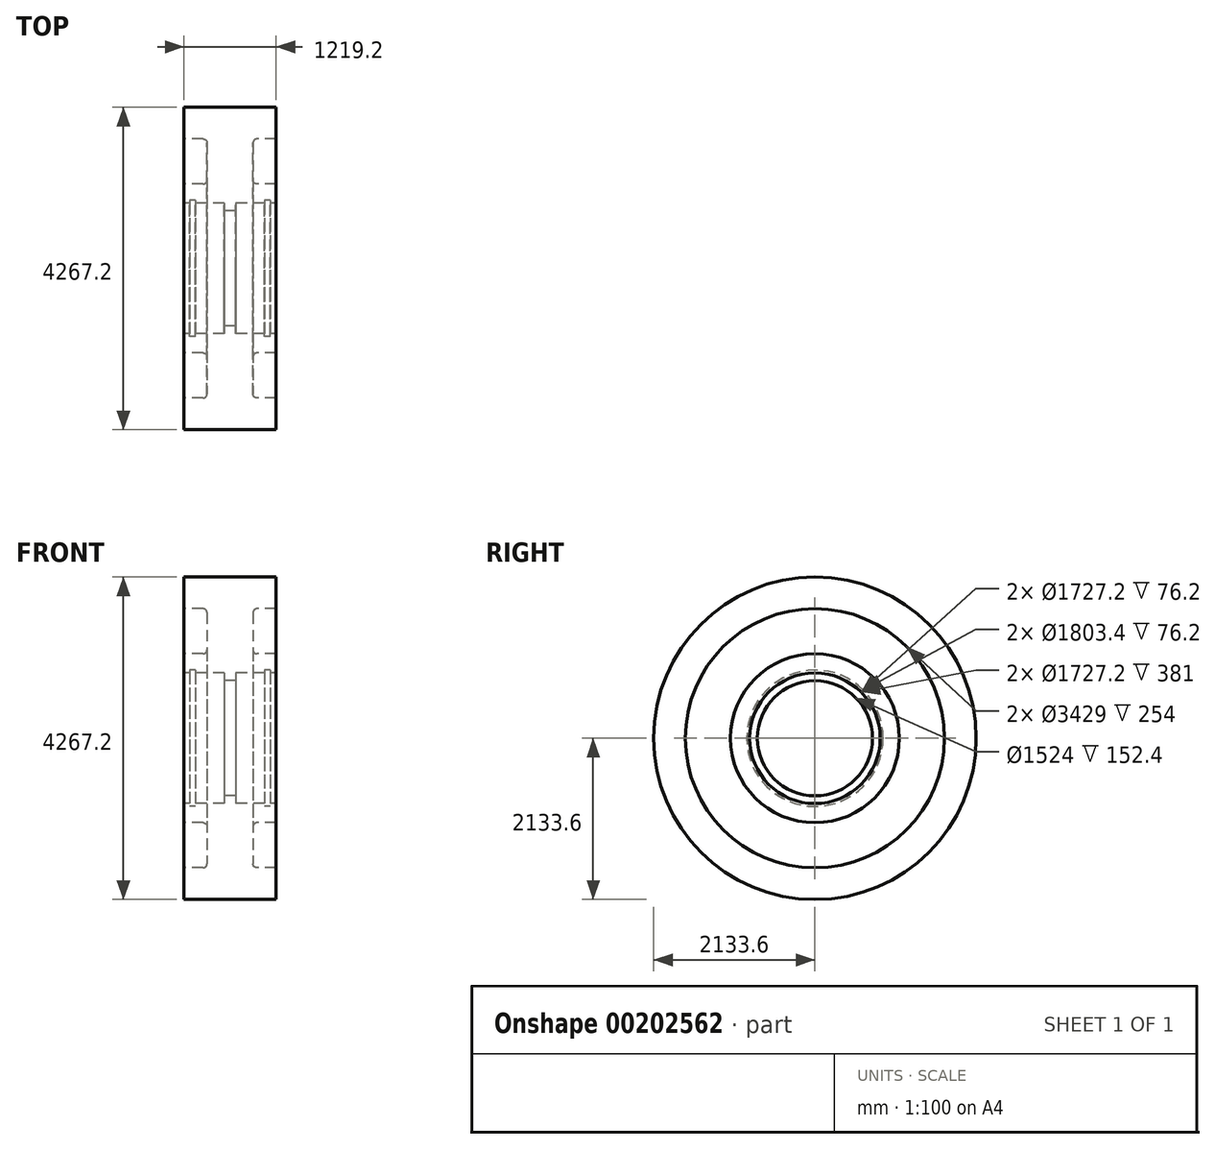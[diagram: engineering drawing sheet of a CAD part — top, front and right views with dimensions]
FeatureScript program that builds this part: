
annotation { "Feature Type Name" : "Feature", "Feature Type Description" : "" }
export const myFeature = defineFeature(function(context is Context, id is Id, definition is map)
    precondition{}
    {
        {
            var Q0;
            Q0=qCreatedBy(makeId("Front.planeOp"),FACE);
            var sketch = newSketch(context, id + "F0", { "sketchPlane" : qUnion([Q0])});
            skLineSegment(sketch, "E0", {"start": v(0, 0) * mm, "end": v(0, 2133.6) * mm, "construction": true});
            skLineSegment(sketch, "E1", {"start": v(0, 2133.6) * mm, "end": v(-609.6, 2133.6) * mm});
            skLineSegment(sketch, "E2", {"start": v(-609.6, 2133.6) * mm, "end": v(-609.6, 1714.5) * mm});
            skLineSegment(sketch, "E3", {"start": v(-609.6, 0) * mm, "end": v(0, 0) * mm, "construction": true});
            skLineSegment(sketch, "E4", {"start": v(-609.6, 863.6) * mm, "end": v(-533.4, 863.6) * mm});
            skLineSegment(sketch, "E5", {"start": v(-533.4, 863.6) * mm, "end": v(-533.4, 901.7) * mm});
            skLineSegment(sketch, "E6", {"start": v(-533.4, 901.7) * mm, "end": v(-457.2, 901.7) * mm});
            skLineSegment(sketch, "E7", {"start": v(-457.2, 901.7) * mm, "end": v(-457.2, 863.6) * mm});
            skLineSegment(sketch, "E8", {"start": v(-457.2, 863.6) * mm, "end": v(-76.2, 863.6) * mm});
            skLineSegment(sketch, "E9", {"start": v(-76.2, 863.6) * mm, "end": v(-76.2, 762) * mm});
            skLineSegment(sketch, "E10", {"start": v(-76.2, 762) * mm, "end": v(0, 762) * mm});
            skLineSegment(sketch, "E11", {"start": v(-609.6, 1714.5) * mm, "end": v(-355.6, 1714.5) * mm});
            skLineSegment(sketch, "E12", {"start": v(-304.8, 1663.7) * mm, "end": v(-304.8, 1168.4) * mm});
            skLineSegment(sketch, "E13", {"start": v(-355.6, 1117.6) * mm, "end": v(-609.6, 1117.6) * mm});
            skLineSegment(sketch, "E14.trimOffspring", {"start": v(-609.6, 1117.6) * mm, "end": v(-609.6, 863.6) * mm});
            skPoint(sketch, "E15.visualSharp", {"position": v(-304.8, 1714.5) * mm});
            skArc(sketch, "E15.filletArc", {"start": v(-304.8, 1663.7) * mm, "mid": v(-319.68, 1699.62) * mm, "end": v(-355.6, 1714.5) * mm});
            skPoint(sketch, "E16.visualSharp", {"position": v(-304.8, 1117.6) * mm});
            skArc(sketch, "E16.filletArc", {"start": v(-355.6, 1117.6) * mm, "mid": v(-319.68, 1132.48) * mm, "end": v(-304.8, 1168.4) * mm});
            skLineSegment(sketch, "E17.MirrorCS", {"start": v(0, 2133.6) * mm, "end": v(609.6, 2133.6) * mm});
            skLineSegment(sketch, "E18.MirrorCS", {"start": v(609.6, 2133.6) * mm, "end": v(609.6, 1714.5) * mm});
            skLineSegment(sketch, "E19.MirrorCS", {"start": v(609.6, 1714.5) * mm, "end": v(355.6, 1714.5) * mm});
            skArc(sketch, "E20.MirrorCS", {"start": v(355.6, 1117.6) * mm, "mid": v(319.68, 1132.48) * mm, "end": v(304.8, 1168.4) * mm});
            skLineSegment(sketch, "E21.MirrorCS", {"start": v(76.2, 762) * mm, "end": v(0, 762) * mm});
            skLineSegment(sketch, "E22.MirrorCS", {"start": v(609.6, 863.6) * mm, "end": v(533.4, 863.6) * mm});
            skLineSegment(sketch, "E23.MirrorCS", {"start": v(533.4, 863.6) * mm, "end": v(533.4, 901.7) * mm});
            skLineSegment(sketch, "E24.MirrorCS", {"start": v(457.2, 901.7) * mm, "end": v(457.2, 863.6) * mm});
            skLineSegment(sketch, "E25.MirrorCS", {"start": v(533.4, 901.7) * mm, "end": v(457.2, 901.7) * mm});
            skLineSegment(sketch, "E26.MirrorCS", {"start": v(609.6, 1117.6) * mm, "end": v(609.6, 863.6) * mm});
            skLineSegment(sketch, "E27.MirrorCS", {"start": v(355.6, 1117.6) * mm, "end": v(609.6, 1117.6) * mm});
            skPoint(sketch, "E28.MirrorP", {"position": v(304.8, 1117.6) * mm});
            skLineSegment(sketch, "E29.MirrorCS", {"start": v(76.2, 863.6) * mm, "end": v(76.2, 762) * mm});
            skLineSegment(sketch, "E30.MirrorCS", {"start": v(304.8, 1663.7) * mm, "end": v(304.8, 1168.4) * mm});
            skLineSegment(sketch, "E31.MirrorCS", {"start": v(457.2, 863.6) * mm, "end": v(76.2, 863.6) * mm});
            skArc(sketch, "E32.MirrorCS", {"start": v(304.8, 1663.7) * mm, "mid": v(319.68, 1699.62) * mm, "end": v(355.6, 1714.5) * mm});
            skSolve(sketch);
        }
        {
            var Q0;
            Q0=makeQuery(id+"F0.imprint","IMPRINT",FACE,{"disambiguationData":[TD([[makeQuery(id+"F0.imprint","IMPRINT",EDGE,{"derivedFrom":sQuery(id+"F0.wireOp",EDGE,"E1")}),1.0]])]});
            var Q1;
            Q1=sQuery(id+"F0.wireOp",EDGE,"E3");
            revolve(context, id + "F1", {"entities" : qUnion([Q0]), "axis" : qUnion([Q1]), "revolveType" : RevolveType.FULL});
        }
    });
